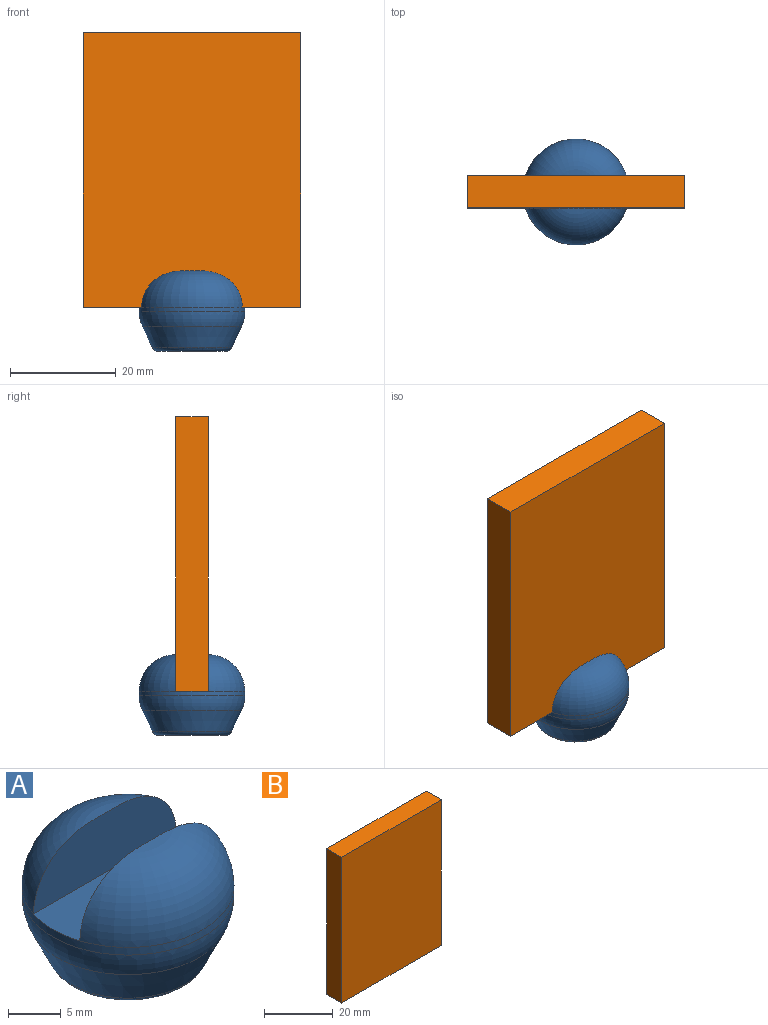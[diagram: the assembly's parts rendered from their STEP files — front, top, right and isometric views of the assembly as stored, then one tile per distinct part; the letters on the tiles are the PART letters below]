
ASSEMBLY  parts=2 mates=1
PART A: 13 faces, bbox 20.1x20.1x15.3 mm
  f0: plane 20.06x6.21mm, normal (0,0,1), area 122.3mm2, adj f1,f2,f8
  f1: plane 19.06x6.93mm, normal (0,-1,0), area 109.6mm2, adj f0,f7
  f2: cylinder r=10.02mm len=20.05mm, axis (0,0,-1), area 55.5mm2, adj f0,f7,f9,f10
  f3: cone r=10.16mm half-angle=25deg, axis (0,0,1), area 238.3mm2, adj f10,f11
  f4: plane 12.78x12.78mm, normal (0,0,-1), area 71.7mm2, adj f11,f12
  f5: plane 0.03x0.03mm, normal (0,0,-1), area 0mm2, adj f6
  f6: cone r=3.49mm half-angle=28.7deg, axis (0,0,-1), area 64.1mm2, adj f5,f12
  f7: torus R=3.1mm, axis (0,0,-1), area 185.3mm2, adj f1,f2
  f8: plane 19.07x6.93mm, normal (0,1,0), area 109.6mm2, adj f0,f9
  f9: torus R=3.1mm, axis (0,0,-1), area 185.3mm2, adj f2,f8
  f10: torus R=3.67mm, axis (0,0,1), area 171mm2, adj f2,f3
  f11: torus R=6.39mm, axis (0,0,-1), area 63.7mm2, adj f3,f4
  f12: torus R=4.24mm, axis (0,0,-1), area 31mm2, adj f4,f6
PART B: 6 faces, bbox 41.2x6.2x52 mm
  f0: plane 41.16x6.2mm, normal (0,0,1), area 255.2mm2, adj f1,f3,f4,f5
  f1: plane 51.99x6.2mm, normal (-1,0,0), area 322.3mm2, adj f0,f2,f4,f5
  f2: plane 41.16x6.2mm, normal (0,0,-1), area 255.2mm2, adj f1,f3,f4,f5
  f3: plane 51.99x6.2mm, normal (1,0,0), area 322.3mm2, adj f0,f2,f4,f5
  f4: plane 51.99x41.16mm, normal (0,-1,0), area 2140mm2, adj f0,f1,f2,f3
  f5: plane 51.99x41.16mm, normal (0,1,0), area 2140mm2, adj f0,f1,f2,f3
PLACE A t=(-23.3,47.71,63.75)mm
PLACE B t=(-21.18,50.81,90)mm
MATE slider A.f6 <-> B.f2  axis (0,0,1) through (-23.3,47.71,65.75)mm
